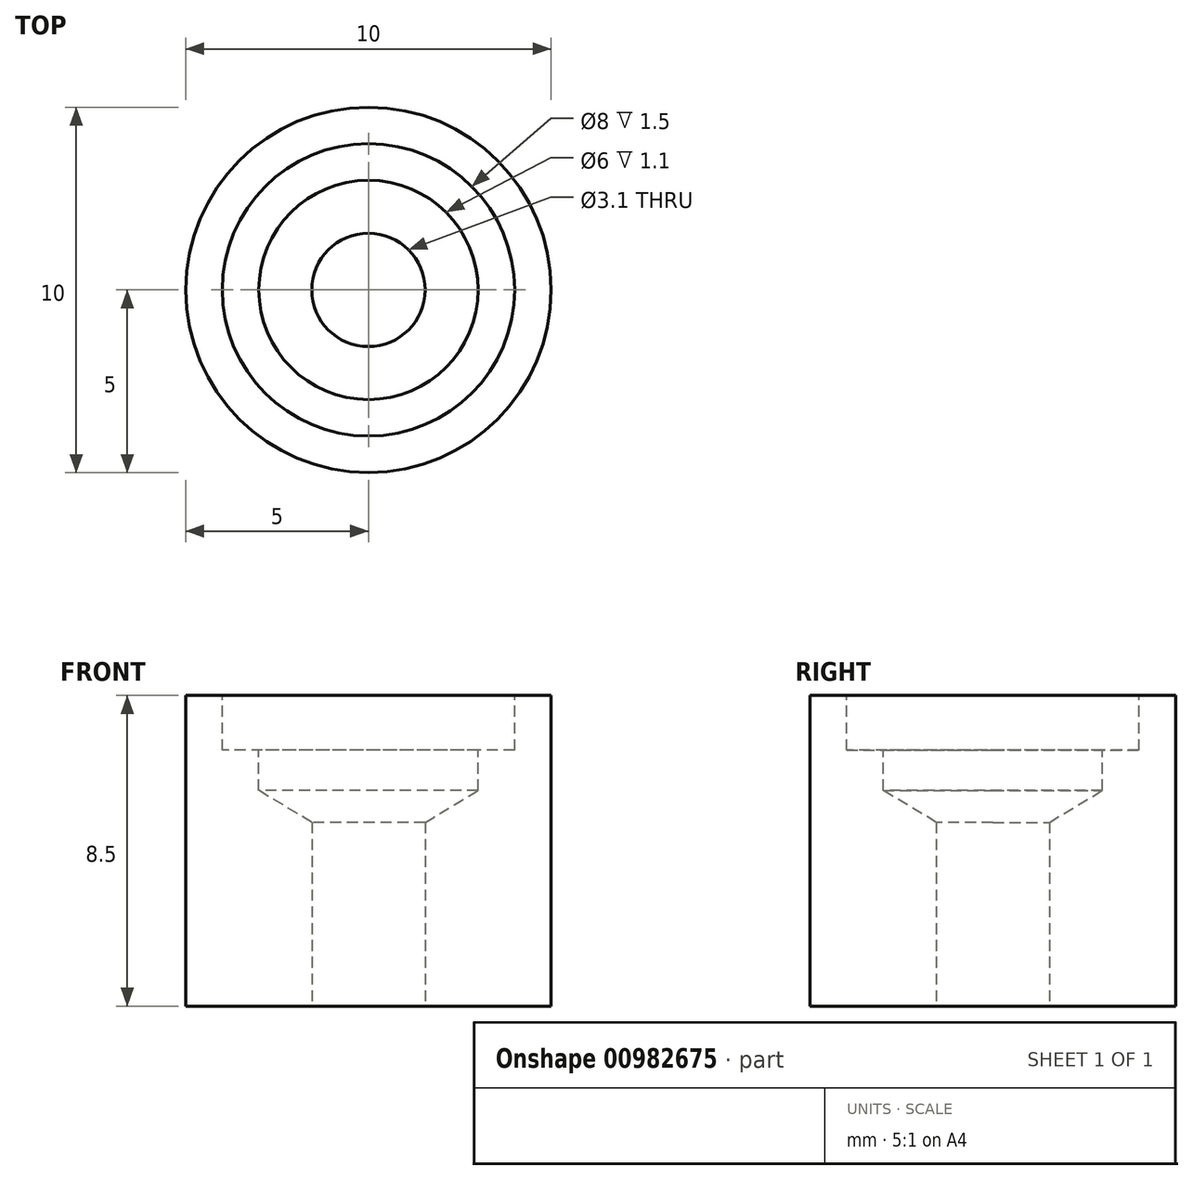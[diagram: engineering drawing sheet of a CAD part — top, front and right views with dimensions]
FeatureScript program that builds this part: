
annotation { "Feature Type Name" : "Feature", "Feature Type Description" : "" }
export const myFeature = defineFeature(function(context is Context, id is Id, definition is map)
    precondition{}
    {
        {
            var Q0;
            Q0=qCreatedBy(makeId("Top.planeOp"),FACE);
            var sketch = newSketch(context, id + "F0", { "sketchPlane" : qUnion([Q0])});
            skCircle(sketch, "E0", {"center": v(0, 0) * mm, "radius": 5 * mm});
            skSolve(sketch);
        }
        {
            var Q0;
            Q0=makeQuery(id+"F0.imprint","IMPRINT",FACE,{"disambiguationData":[TD([[makeQuery(id+"F0.imprint","IMPRINT",EDGE,{"derivedFrom":sQuery(id+"F0.wireOp",EDGE,"E0")}),1.0]])]});
            extrude(context, id + "F1", {"entities" : qUnion([Q0]), "depth" : 8.5 * mm, "offsetDistance" : 25 * mm});
        }
        {
            var Q0;
            Q0=makeQuery(id+"F1.opExtrude","CAP_FACE",FACE,{"disambiguationData":[OSD([sQuery(id+"F0.wireOp",EDGE,"E0")])],"isStart":false});
            var sketch = newSketch(context, id + "F2", { "sketchPlane" : qUnion([Q0])});
            skCircle(sketch, "E1", {"center": v(0, 0) * mm, "radius": 4 * mm});
            skSolve(sketch);
        }
        {
            var Q0;
            Q0=makeQuery(id+"F2.imprint","IMPRINT",FACE,{"disambiguationData":[TD([[makeQuery(id+"F2.imprint","IMPRINT",EDGE,{"derivedFrom":sQuery(id+"F2.wireOp",EDGE,"E1")}),1.0]])]});
            extrude(context, id + "F3", {"entities" : qUnion([Q0]), "operationType" : NewBodyOperationType.REMOVE, "oppositeDirection" : true, "depth" : 1.5 * mm, "offsetDistance" : 25 * mm});
        }
        {
            var Q0;
            Q0=sQuery(id+"F2.wireOp",VERTEX,"E1.center");
            var Q1;
            Q1=makeQuery(id+"F1.opExtrude","SWEPT_BODY",BODY,{"disambiguationData":[OSD([sQuery(id+"F0.wireOp",EDGE,"E0")])]});
            hole(context, id + "F4", {"style" : HoleStyle.C_SINK, "endStyle" : HoleEndStyle.BLIND, "holeDiameter" : 6 * mm, "cSinkDiameter" : 6 * mm, "cSinkAngle" : 90 * degree, "majorDiameter" : 5 * mm, "holeDepth" : 2.6 * mm, "isTappedThrough" : true, "tappedDepth" : 12 * mm, "tapClearance" : 3, "startFromSketch" : true, "locations" : qUnion([Q0]), "scope" : qUnion([Q1])});
        }
        {
            var Q0;
            Q0=makeQuery(id+"F1.opExtrude","CAP_FACE",FACE,{"disambiguationData":[OSD([sQuery(id+"F0.wireOp",EDGE,"E0")])],"isStart":true});
            var sketch = newSketch(context, id + "F5", { "sketchPlane" : qUnion([Q0])});
            skCircle(sketch, "E2", {"center": v(0, 0) * mm, "radius": 1.55 * mm});
            skSolve(sketch);
        }
        {
            var Q0;
            Q0=makeQuery(id+"F5.imprint","IMPRINT",FACE,{"disambiguationData":[TD([[makeQuery(id+"F5.imprint","IMPRINT",EDGE,{"derivedFrom":sQuery(id+"F5.wireOp",EDGE,"E2")}),1.0]])]});
            extrude(context, id + "F6", {"entities" : qUnion([Q0]), "operationType" : NewBodyOperationType.REMOVE, "oppositeDirection" : true, "depth" : 25 * mm, "offsetDistance" : 25 * mm});
        }
    });
